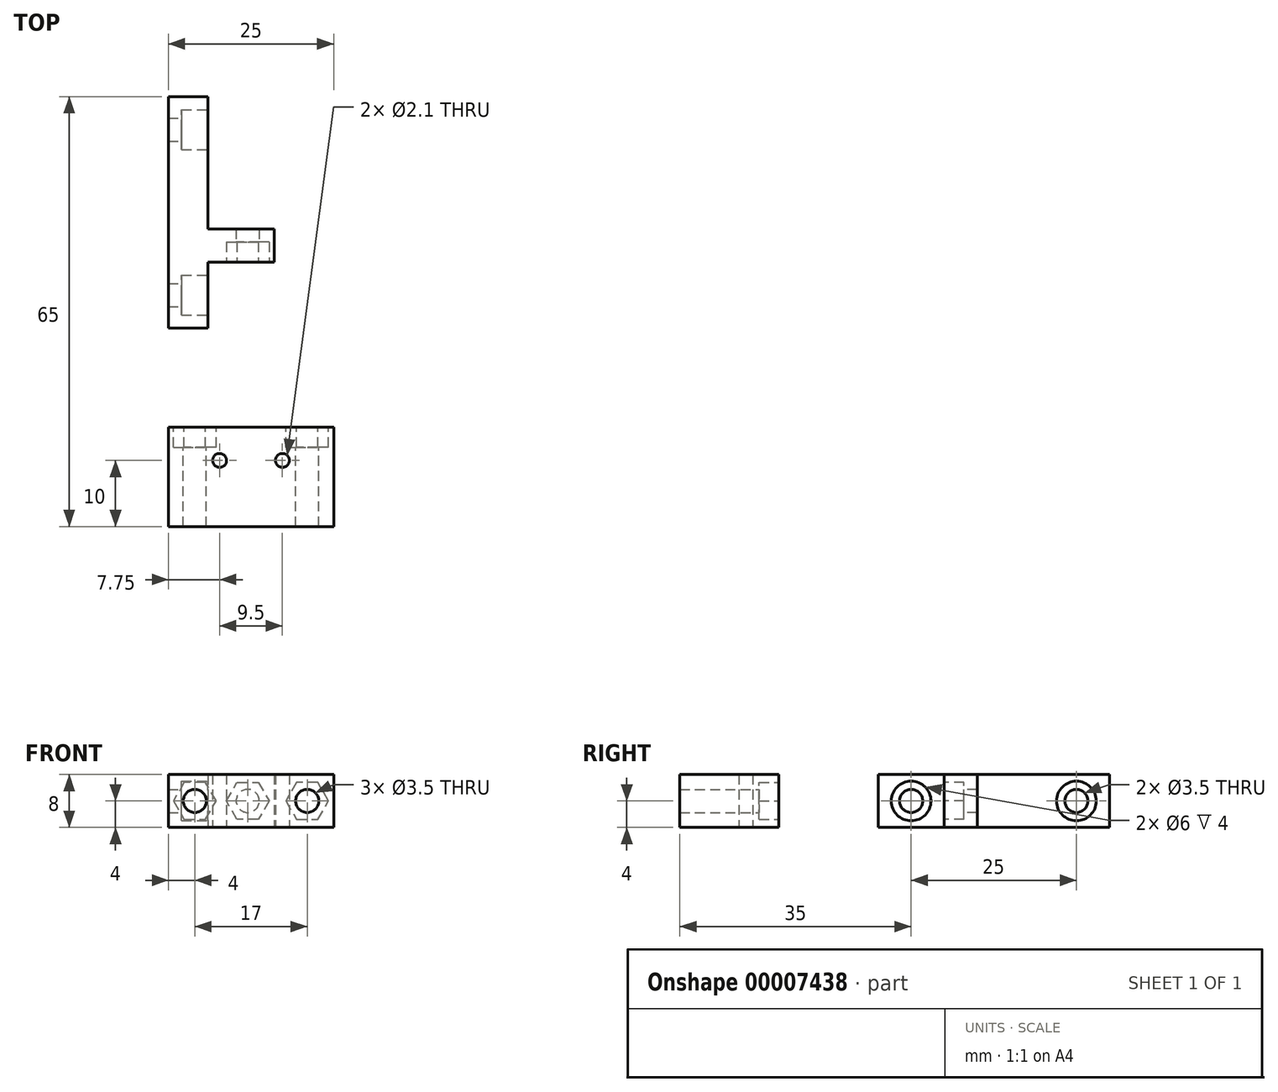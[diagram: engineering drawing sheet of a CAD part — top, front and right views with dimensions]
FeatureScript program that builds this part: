
annotation { "Feature Type Name" : "Feature", "Feature Type Description" : "" }
export const myFeature = defineFeature(function(context is Context, id is Id, definition is map)
    precondition{}
    {
        {
            var Q0;
            Q0=qCreatedBy(makeId("Top.planeOp"),FACE);
            var sketch = newSketch(context, id + "F0", { "sketchPlane" : qUnion([Q0])});
            skLineSegment(sketch, "E0", {"start": v(0, 65) * mm, "end": v(0, 40) * mm});
            skLineSegment(sketch, "E1", {"start": v(16, 40) * mm, "end": v(16, 45) * mm});
            skLineSegment(sketch, "E2", {"start": v(16, 45) * mm, "end": v(6, 45) * mm});
            skLineSegment(sketch, "E3", {"start": v(6, 45) * mm, "end": v(6, 65) * mm});
            skLineSegment(sketch, "E4", {"start": v(6, 65) * mm, "end": v(0, 65) * mm});
            skLineSegment(sketch, "E5", {"start": v(0, 0) * mm, "end": v(0, 15) * mm});
            skLineSegment(sketch, "E6", {"start": v(0, 15) * mm, "end": v(25, 15) * mm});
            skLineSegment(sketch, "E7", {"start": v(25, 15) * mm, "end": v(25, 0) * mm});
            skLineSegment(sketch, "E8", {"start": v(25, 0) * mm, "end": v(0, 0) * mm});
            skLineSegment(sketch, "E9", {"start": v(7.75, 10) * mm, "end": v(17.25, 10) * mm, "construction": true});
            skCircle(sketch, "E10", {"center": v(7.75, 10) * mm, "radius": 1.05 * mm});
            skCircle(sketch, "E11", {"center": v(17.25, 10) * mm, "radius": 1.05 * mm});
            skPoint(sketch, "E12", {"position": v(12.5, 10) * mm});
            skLineSegment(sketch, "E13", {"start": v(0, 40) * mm, "end": v(0, 30) * mm});
            skLineSegment(sketch, "E14", {"start": v(0, 30) * mm, "end": v(6, 30) * mm});
            skLineSegment(sketch, "E15", {"start": v(6, 30) * mm, "end": v(6, 40) * mm});
            skLineSegment(sketch, "E16", {"start": v(6, 40) * mm, "end": v(16, 40) * mm});
            skSolve(sketch);
        }
        {
            var Q0;
            Q0=makeQuery(id+"F0.imprint","IMPRINT",FACE,{"disambiguationData":[TD([[makeQuery(id+"F0.imprint","IMPRINT",EDGE,{"derivedFrom":sQuery(id+"F0.wireOp",EDGE,"E5")}),-1.0]])]});
            extrude(context, id + "F1", {"entities" : qUnion([Q0]), "depth" : 8 * mm});
        }
        {
            var Q0;
            Q0=makeQuery(id+"F1.opExtrude","SWEPT_FACE",FACE,{"disambiguationData":[OSD([sQuery(id+"F0.wireOp",EDGE,"E6")])]});
            var sketch = newSketch(context, id + "F2", { "sketchPlane" : qUnion([Q0])});
            skCircle(sketch, "E17", {"center": v(-4, 4) * mm, "radius": 1.75 * mm});
            skLineSegment(sketch, "E18", {"start": v(-4, 4) * mm, "end": v(-21, 4) * mm, "construction": true});
            skCircle(sketch, "E19", {"center": v(-21, 4) * mm, "radius": 1.75 * mm});
            skCircle(sketch, "E20.cCircle", {"center": v(-21, 4) * mm, "radius": 2.8 * mm, "construction": true});
            skLineSegment(sketch, "E20.0", {"start": v(-22.62, 6.8) * mm, "end": v(-19.38, 6.8) * mm});
            skLineSegment(sketch, "E20.1", {"start": v(-19.38, 6.8) * mm, "end": v(-17.77, 4) * mm});
            skLineSegment(sketch, "E20.2", {"start": v(-17.77, 4) * mm, "end": v(-19.38, 1.2) * mm});
            skLineSegment(sketch, "E20.3", {"start": v(-19.38, 1.2) * mm, "end": v(-22.62, 1.2) * mm});
            skLineSegment(sketch, "E20.4", {"start": v(-22.62, 1.2) * mm, "end": v(-24.23, 4) * mm});
            skLineSegment(sketch, "E20.5", {"start": v(-24.23, 4) * mm, "end": v(-22.62, 6.8) * mm});
            skPoint(sketch, "E20.0.midPoint", {"position": v(-21, 6.8) * mm});
            skCircle(sketch, "E21.cCircle", {"center": v(-4, 4) * mm, "radius": 2.8 * mm, "construction": true});
            skLineSegment(sketch, "E21.0", {"start": v(-5.62, 6.8) * mm, "end": v(-2.38, 6.8) * mm});
            skLineSegment(sketch, "E21.1", {"start": v(-2.38, 6.8) * mm, "end": v(-0.77, 4) * mm});
            skLineSegment(sketch, "E21.2", {"start": v(-0.77, 4) * mm, "end": v(-2.38, 1.2) * mm});
            skLineSegment(sketch, "E21.3", {"start": v(-2.38, 1.2) * mm, "end": v(-5.62, 1.2) * mm});
            skLineSegment(sketch, "E21.4", {"start": v(-5.62, 1.2) * mm, "end": v(-7.23, 4) * mm});
            skLineSegment(sketch, "E21.5", {"start": v(-7.23, 4) * mm, "end": v(-5.62, 6.8) * mm});
            skPoint(sketch, "E21.0.midPoint", {"position": v(-4, 6.8) * mm});
            skSolve(sketch);
        }
        {
            var Q0;
            Q0=makeQuery(id+"F2.imprint","IMPRINT",FACE,{"disambiguationData":[TD([[makeQuery(id+"F2.imprint","IMPRINT",EDGE,{"derivedFrom":sQuery(id+"F2.wireOp",EDGE,"E19")}),1.0]])]});
            var Q1;
            Q1=makeQuery(id+"F2.imprint","IMPRINT",FACE,{"disambiguationData":[TD([[makeQuery(id+"F2.imprint","IMPRINT",EDGE,{"derivedFrom":sQuery(id+"F2.wireOp",EDGE,"E17")}),1.0]])]});
            extrude(context, id + "F3", {"entities" : qUnion([Q0, Q1]), "operationType" : NewBodyOperationType.REMOVE, "endBound" : BoundingType.THROUGH_ALL, "oppositeDirection" : true, "depth" : 25 * mm});
        }
        {
            var Q0;
            Q0=makeQuery(id+"F2.imprint","IMPRINT",FACE,{"disambiguationData":[TD([[makeQuery(id+"F2.imprint","IMPRINT",EDGE,{"derivedFrom":sQuery(id+"F2.wireOp",EDGE,"E17")}),-1.0]])]});
            var Q1;
            Q1=makeQuery(id+"F2.imprint","IMPRINT",FACE,{"disambiguationData":[TD([[makeQuery(id+"F2.imprint","IMPRINT",EDGE,{"derivedFrom":sQuery(id+"F2.wireOp",EDGE,"E19")}),-1.0]])]});
            extrude(context, id + "F4", {"entities" : qUnion([Q0, Q1]), "operationType" : NewBodyOperationType.REMOVE, "oppositeDirection" : true, "depth" : 3 * mm});
        }
        {
            var Q0;
            Q0=makeQuery(id+"F0.imprint","IMPRINT",FACE,{"disambiguationData":[TD([[makeQuery(id+"F0.imprint","IMPRINT",EDGE,{"derivedFrom":sQuery(id+"F0.wireOp",EDGE,"E0")}),1.0]])]});
            extrude(context, id + "F5", {"entities" : qUnion([Q0]), "depth" : 8 * mm});
        }
        {
            var Q0;
            Q0=makeQuery(id+"F5.opExtrude","SWEPT_FACE",FACE,{"disambiguationData":[OSD([sQuery(id+"F0.wireOp",EDGE,"E3")])]});
            var sketch = newSketch(context, id + "F6", { "sketchPlane" : qUnion([Q0])});
            skCircle(sketch, "E22", {"center": v(60, 4) * mm, "radius": 3 * mm});
            skCircle(sketch, "E23", {"center": v(60, 4) * mm, "radius": 1.75 * mm});
            skCircle(sketch, "E24", {"center": v(35, 4) * mm, "radius": 1.75 * mm});
            skCircle(sketch, "E25", {"center": v(35, 4) * mm, "radius": 3 * mm});
            skLineSegment(sketch, "E26", {"start": v(35, 4) * mm, "end": v(60, 4) * mm, "construction": true});
            skSolve(sketch);
        }
        {
            var Q0;
            Q0=makeQuery(id+"F6.imprint","IMPRINT",FACE,{"disambiguationData":[TD([[makeQuery(id+"F6.imprint","IMPRINT",EDGE,{"derivedFrom":sQuery(id+"F6.wireOp",EDGE,"E23")}),1.0]])]});
            var Q1;
            Q1=makeQuery(id+"F6.imprint","IMPRINT",FACE,{"disambiguationData":[TD([[makeQuery(id+"F6.imprint","IMPRINT",EDGE,{"derivedFrom":sQuery(id+"F6.wireOp",EDGE,"E24")}),1.0]])]});
            extrude(context, id + "F7", {"entities" : qUnion([Q0, Q1]), "operationType" : NewBodyOperationType.REMOVE, "endBound" : BoundingType.THROUGH_ALL, "oppositeDirection" : true, "depth" : 25 * mm});
        }
        {
            var Q0;
            Q0=makeQuery(id+"F6.imprint","IMPRINT",FACE,{"disambiguationData":[TD([[makeQuery(id+"F6.imprint","IMPRINT",EDGE,{"derivedFrom":sQuery(id+"F6.wireOp",EDGE,"E22")}),1.0]])]});
            var Q1;
            Q1=makeQuery(id+"F6.imprint","IMPRINT",FACE,{"disambiguationData":[TD([[makeQuery(id+"F6.imprint","IMPRINT",EDGE,{"derivedFrom":sQuery(id+"F6.wireOp",EDGE,"E24")}),-1.0]])]});
            extrude(context, id + "F8", {"entities" : qUnion([Q0, Q1]), "operationType" : NewBodyOperationType.REMOVE, "oppositeDirection" : true, "depth" : 4 * mm});
        }
        {
            var Q0;
            Q0=makeQuery(id+"F5.opExtrude","SWEPT_FACE",FACE,{"disambiguationData":[OSD([sQuery(id+"F0.wireOp",EDGE,"E16")])]});
            var sketch = newSketch(context, id + "F9", { "sketchPlane" : qUnion([Q0])});
            skCircle(sketch, "E27", {"center": v(12, 4) * mm, "radius": 1.75 * mm});
            skCircle(sketch, "E28.cCircle", {"center": v(12, 4) * mm, "radius": 2.8 * mm, "construction": true});
            skLineSegment(sketch, "E28.0", {"start": v(10.38, 6.8) * mm, "end": v(13.62, 6.8) * mm});
            skLineSegment(sketch, "E28.1", {"start": v(13.62, 6.8) * mm, "end": v(15.23, 4) * mm});
            skLineSegment(sketch, "E28.2", {"start": v(15.23, 4) * mm, "end": v(13.62, 1.2) * mm});
            skLineSegment(sketch, "E28.3", {"start": v(13.62, 1.2) * mm, "end": v(10.38, 1.2) * mm});
            skLineSegment(sketch, "E28.4", {"start": v(10.38, 1.2) * mm, "end": v(8.77, 4) * mm});
            skLineSegment(sketch, "E28.5", {"start": v(8.77, 4) * mm, "end": v(10.38, 6.8) * mm});
            skPoint(sketch, "E28.0.midPoint", {"position": v(12, 6.8) * mm});
            skSolve(sketch);
        }
        {
            var Q0;
            Q0=makeQuery(id+"F9.imprint","IMPRINT",FACE,{"disambiguationData":[TD([[makeQuery(id+"F9.imprint","IMPRINT",EDGE,{"derivedFrom":sQuery(id+"F9.wireOp",EDGE,"E27")}),1.0]])]});
            extrude(context, id + "F10", {"entities" : qUnion([Q0]), "operationType" : NewBodyOperationType.REMOVE, "oppositeDirection" : true, "depth" : 25 * mm});
        }
        {
            var Q0;
            Q0=makeQuery(id+"F9.imprint","IMPRINT",FACE,{"disambiguationData":[TD([[makeQuery(id+"F9.imprint","IMPRINT",EDGE,{"derivedFrom":sQuery(id+"F9.wireOp",EDGE,"E27")}),-1.0]])]});
            extrude(context, id + "F11", {"entities" : qUnion([Q0]), "operationType" : NewBodyOperationType.REMOVE, "oppositeDirection" : true, "depth" : 3 * mm});
        }
    });
